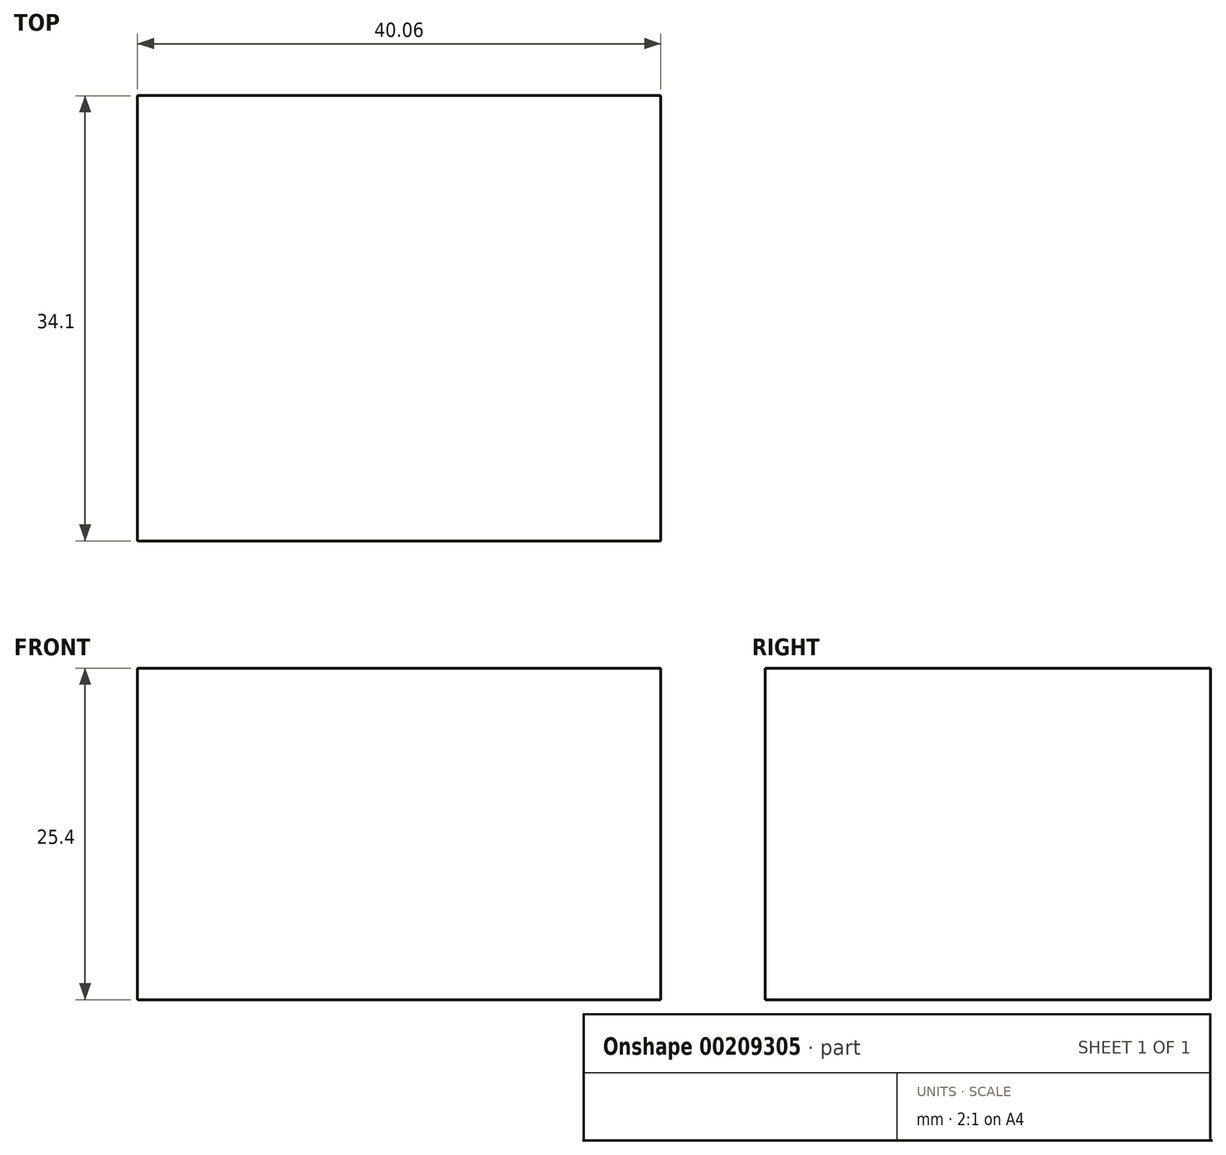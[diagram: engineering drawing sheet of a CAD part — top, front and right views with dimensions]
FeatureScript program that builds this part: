
annotation { "Feature Type Name" : "Feature", "Feature Type Description" : "" }
export const myFeature = defineFeature(function(context is Context, id is Id, definition is map)
    precondition{}
    {
        {
            var Q0;
            Q0=qCreatedBy(makeId("Top.planeOp"),FACE);
            var sketch = newSketch(context, id + "F0", { "sketchPlane" : qUnion([Q0])});
            skLineSegment(sketch, "E0.bottom", {"start": v(-20.03, 17.05) * mm, "end": v(20.03, 17.05) * mm});
            skLineSegment(sketch, "E0.top", {"start": v(-20.03, -17.05) * mm, "end": v(20.03, -17.05) * mm});
            skLineSegment(sketch, "E0.left", {"start": v(-20.03, 17.05) * mm, "end": v(-20.03, -17.05) * mm});
            skLineSegment(sketch, "E0.right", {"start": v(20.03, 17.05) * mm, "end": v(20.03, -17.05) * mm});
            skPoint(sketch, "E0.middle", {"position": v(0, 0) * mm});
            skSolve(sketch);
        }
        {
            var Q0;
            Q0=makeQuery(id+"F0.imprint","IMPRINT",FACE,{"disambiguationData":[TD([[makeQuery(id+"F0.imprint","IMPRINT",EDGE,{"derivedFrom":sQuery(id+"F0.wireOp",EDGE,"E0.bottom")}),-1.0]])]});
            extrude(context, id + "F1", {"entities" : qUnion([Q0]), "depth" : 25.4 * mm});
        }
    });
